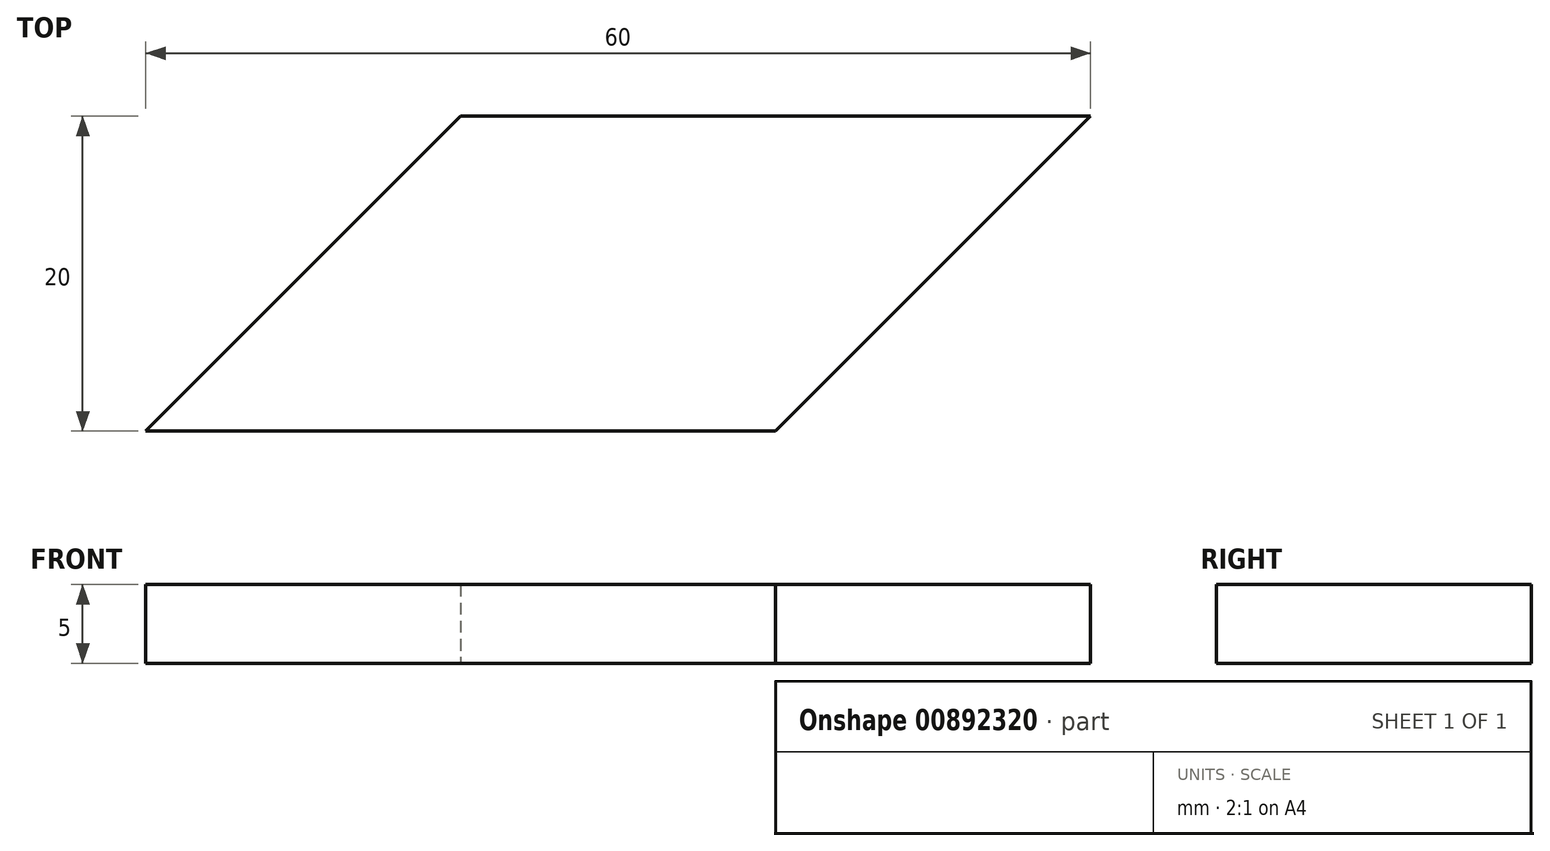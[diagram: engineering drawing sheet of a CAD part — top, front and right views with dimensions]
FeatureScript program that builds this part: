
annotation { "Feature Type Name" : "Feature", "Feature Type Description" : "" }
export const myFeature = defineFeature(function(context is Context, id is Id, definition is map)
    precondition{}
    {
        {
            var Q0;
            Q0=qCreatedBy(makeId("Top.planeOp"),FACE);
            var sketch = newSketch(context, id + "F0", { "sketchPlane" : qUnion([Q0])});
            skLineSegment(sketch, "E0.bottom", {"start": v(10, -20) * mm, "end": v(-30, -20) * mm});
            skPoint(sketch, "E0.middle", {"position": v(0, 0) * mm});
            skLineSegment(sketch, "E1", {"start": v(-30, -20) * mm, "end": v(-10, 0) * mm});
            skLineSegment(sketch, "E2", {"start": v(10, -20) * mm, "end": v(30, 0) * mm});
            skLineSegment(sketch, "E3", {"start": v(-10, 0) * mm, "end": v(31.07, 0) * mm});
            skPoint(sketch, "E4.orphan", {"position": v(-30, 20) * mm});
            skPoint(sketch, "E5.orphan", {"position": v(30, 20) * mm});
            skPoint(sketch, "E6.orphan", {"position": v(30, -20) * mm});
            skSolve(sketch);
        }
        {
            var Q0;
            Q0=makeQuery(id+"F0.imprint","IMPRINT",FACE,{"disambiguationData":[TD([[makeQuery(id+"F0.imprint","IMPRINT",EDGE,{"derivedFrom":sQuery(id+"F0.wireOp",EDGE,"E0.bottom")}),-1.0]])]});
            extrude(context, id + "F1", {"entities" : qUnion([Q0]), "depth" : 5 * mm, "offsetDistance" : 25.4 * mm});
        }
    });
